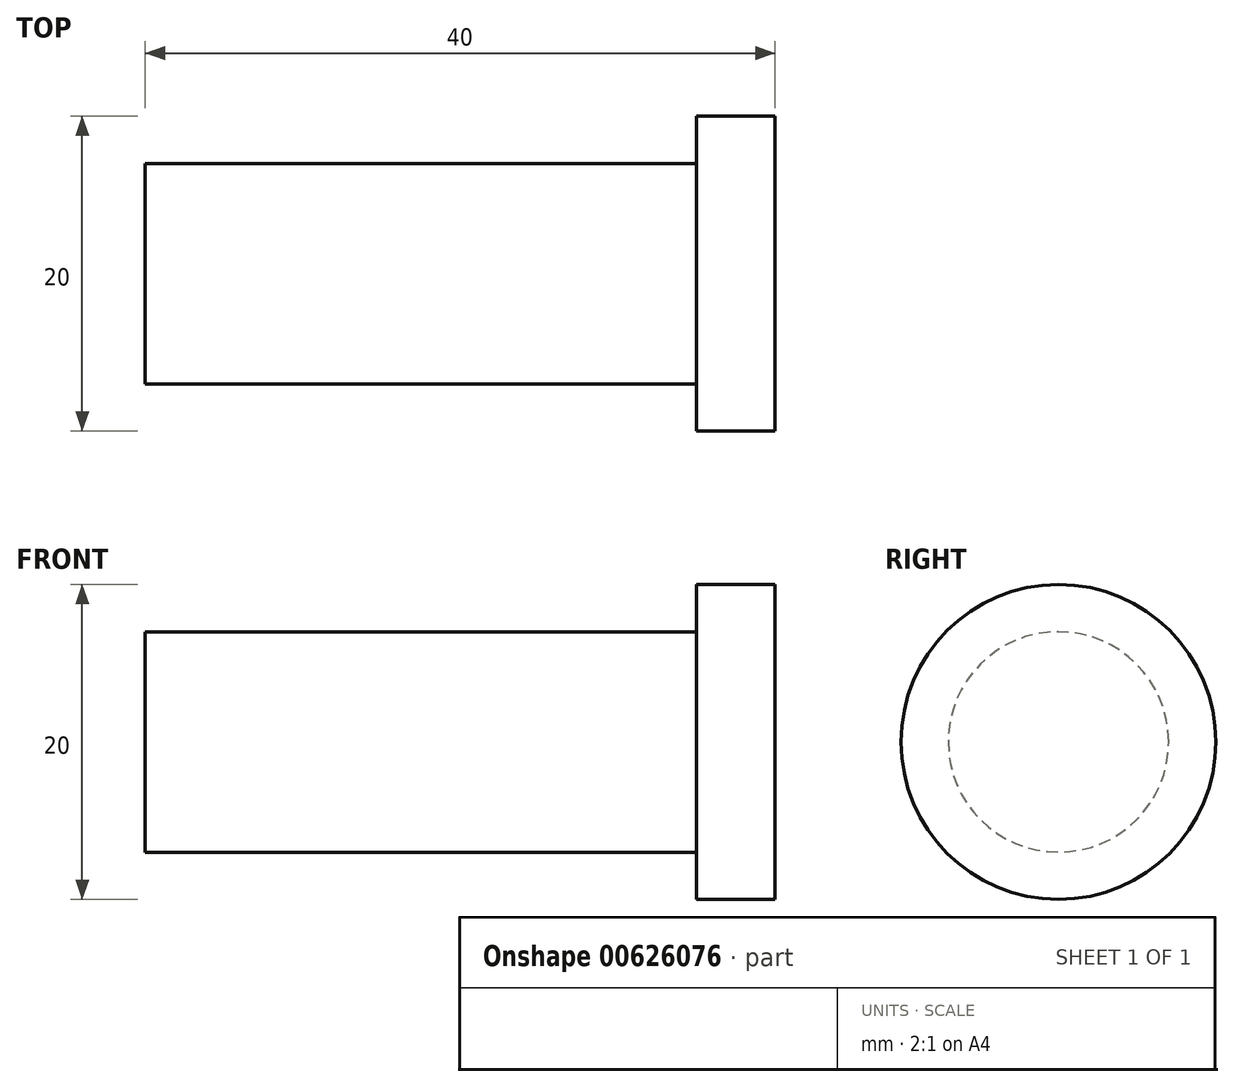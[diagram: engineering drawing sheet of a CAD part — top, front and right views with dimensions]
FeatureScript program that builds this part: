
annotation { "Feature Type Name" : "Feature", "Feature Type Description" : "" }
export const myFeature = defineFeature(function(context is Context, id is Id, definition is map)
    precondition{}
    {
        {
            var Q0;
            Q0=qCreatedBy(makeId("Front.planeOp"),FACE);
            var sketch = newSketch(context, id + "F0", { "sketchPlane" : qUnion([Q0])});
            skLineSegment(sketch, "E0", {"start": v(-40, 0) * mm, "end": v(0, 0) * mm});
            skLineSegment(sketch, "E1", {"start": v(0, 0) * mm, "end": v(0, 10) * mm});
            skLineSegment(sketch, "E2", {"start": v(0, 10) * mm, "end": v(-5, 10) * mm});
            skLineSegment(sketch, "E3", {"start": v(-5, 10) * mm, "end": v(-5, 7) * mm});
            skLineSegment(sketch, "E4", {"start": v(-5, 7) * mm, "end": v(-40, 7) * mm});
            skLineSegment(sketch, "E5", {"start": v(-40, 7) * mm, "end": v(-40, 0) * mm});
            skSolve(sketch);
        }
        {
            var Q0;
            Q0=makeQuery(id+"F0.imprint","IMPRINT",FACE,{"disambiguationData":[TD([[makeQuery(id+"F0.imprint","IMPRINT",EDGE,{"derivedFrom":sQuery(id+"F0.wireOp",EDGE,"E0")}),1.0]])]});
            var Q1;
            Q1=sQuery(id+"F0.wireOp",EDGE,"E0");
            revolve(context, id + "F1", {"surfaceOperationType" : NewSurfaceOperationType.NEW, "entities" : qUnion([Q0]), "axis" : qUnion([Q1]), "revolveType" : RevolveType.FULL});
        }
    });
